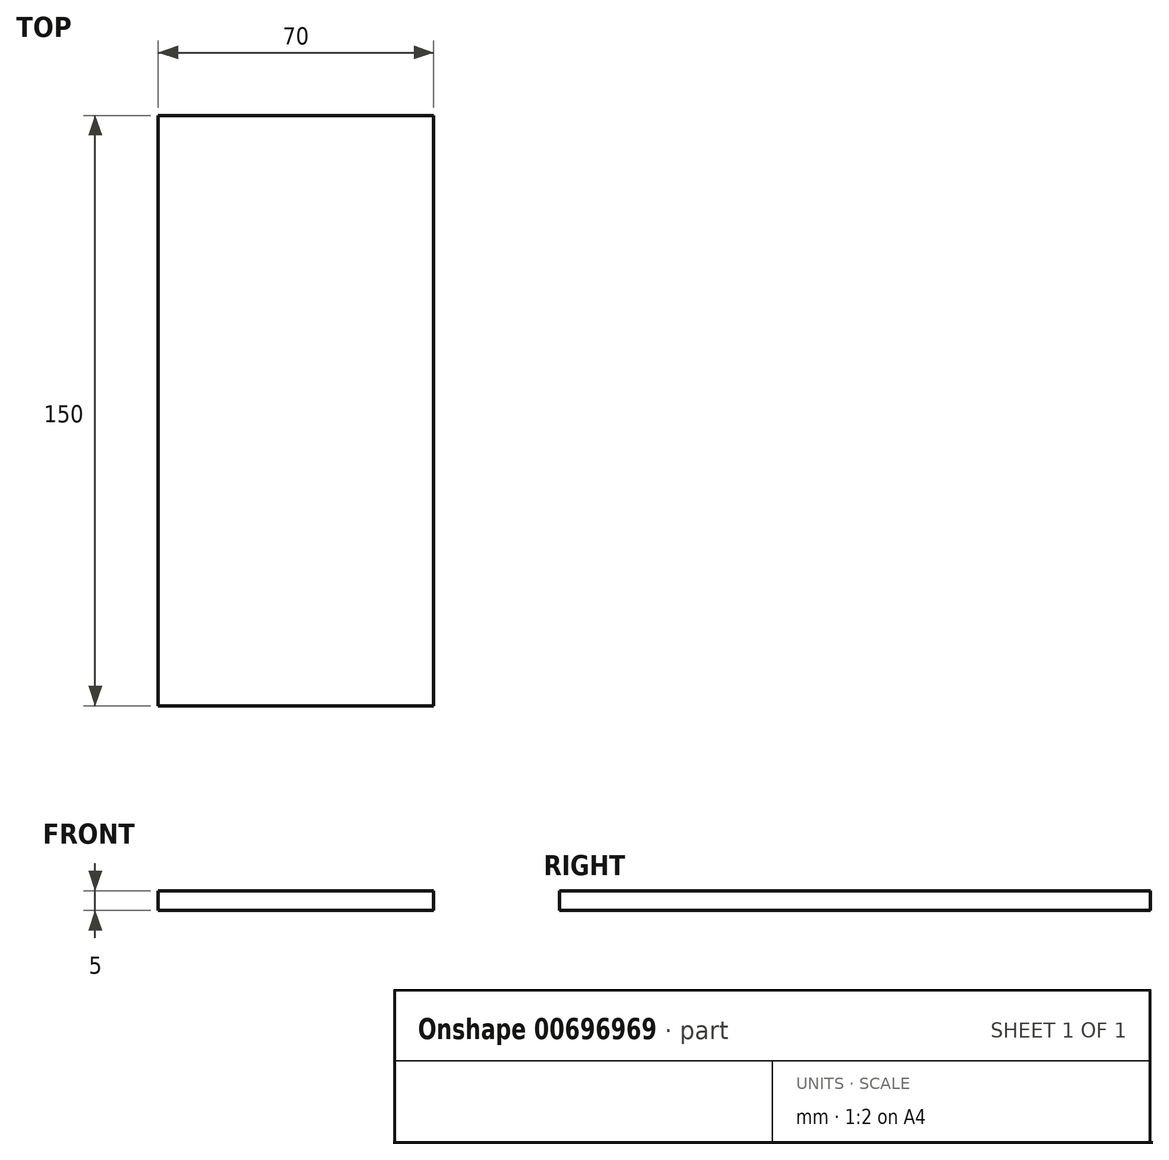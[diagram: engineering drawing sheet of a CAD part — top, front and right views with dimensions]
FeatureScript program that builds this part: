
annotation { "Feature Type Name" : "Feature", "Feature Type Description" : "" }
export const myFeature = defineFeature(function(context is Context, id is Id, definition is map)
    precondition{}
    {
        {
            var Q0;
            Q0=qCreatedBy(makeId("Top.planeOp"),FACE);
            var sketch = newSketch(context, id + "F0", { "sketchPlane" : qUnion([Q0])});
            skLineSegment(sketch, "E0.bottom", {"start": v(-38.52, 105.76) * mm, "end": v(31.48, 105.76) * mm});
            skLineSegment(sketch, "E0.top", {"start": v(-38.52, -44.24) * mm, "end": v(31.48, -44.24) * mm});
            skLineSegment(sketch, "E0.left", {"start": v(-38.52, 105.76) * mm, "end": v(-38.52, -44.24) * mm});
            skLineSegment(sketch, "E0.right", {"start": v(31.48, 105.76) * mm, "end": v(31.48, -44.24) * mm});
            skLineSegment(sketch, "E1", {"start": v(-14.53, 16.44) * mm, "end": v(13.47, -24.99) * mm});
            skLineSegment(sketch, "E2", {"start": v(11.05, 16.5) * mm, "end": v(-16.45, -25.25) * mm});
            skSolve(sketch);
        }
        {
            var Q0;
            Q0=makeQuery(id+"F0.imprint","IMPRINT",FACE,{"disambiguationData":[TD([[makeQuery(id+"F0.imprint","IMPRINT",EDGE,{"derivedFrom":sQuery(id+"F0.wireOp",EDGE,"E0.bottom")}),-1.0]])]});
            extrude(context, id + "F1", {"entities" : qUnion([Q0]), "oppositeDirection" : true, "depth" : 5 * mm, "offsetDistance" : 25 * mm});
        }
    });
